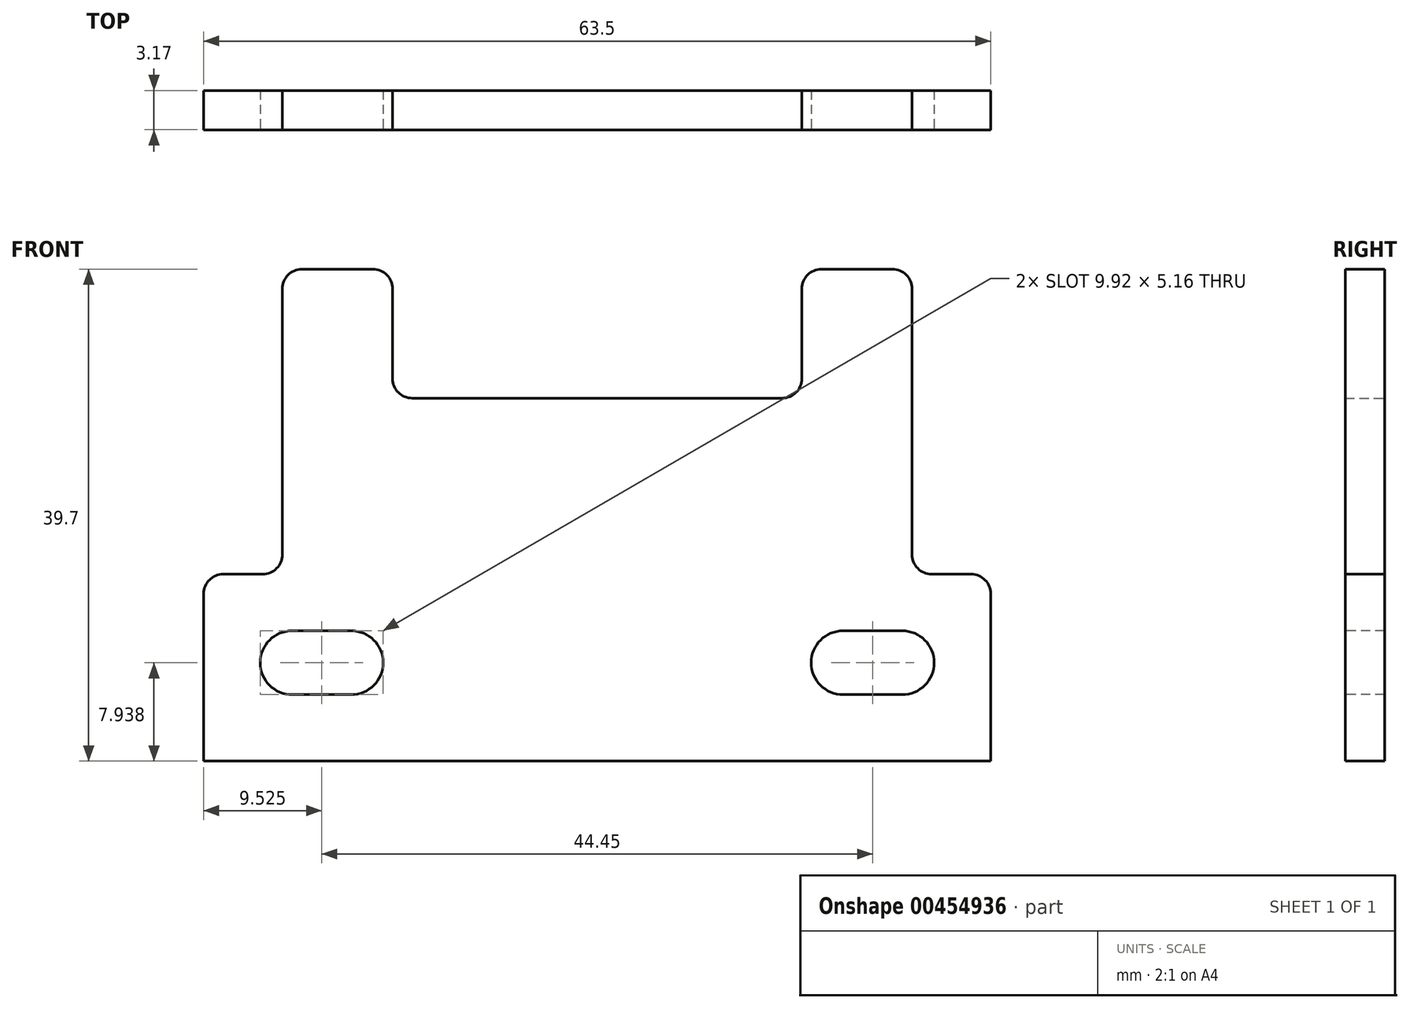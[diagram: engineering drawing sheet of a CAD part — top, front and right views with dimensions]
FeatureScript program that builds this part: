
annotation { "Feature Type Name" : "Feature", "Feature Type Description" : "" }
export const myFeature = defineFeature(function(context is Context, id is Id, definition is map)
    precondition{}
    {
        {
            var Q0;
            Q0=qCreatedBy(makeId("Front.planeOp"),FACE);
            var sketch = newSketch(context, id + "F0", { "sketchPlane" : qUnion([Q0])});
            skLineSegment(sketch, "E0", {"start": v(0, 0) * mm, "end": v(63.5, 0) * mm});
            skLineSegment(sketch, "E1", {"start": v(63.5, 0) * mm, "end": v(63.5, 15.08) * mm});
            skLineSegment(sketch, "E2", {"start": v(63.5, 15.08) * mm, "end": v(57.15, 15.08) * mm});
            skLineSegment(sketch, "E3", {"start": v(57.15, 15.08) * mm, "end": v(57.15, 39.7) * mm});
            skLineSegment(sketch, "E4", {"start": v(57.15, 39.7) * mm, "end": v(48.26, 39.7) * mm});
            skLineSegment(sketch, "E5", {"start": v(48.26, 39.7) * mm, "end": v(48.26, 29.29) * mm});
            skLineSegment(sketch, "E6", {"start": v(15.24, 29.29) * mm, "end": v(15.24, 39.7) * mm});
            skLineSegment(sketch, "E7", {"start": v(15.24, 39.7) * mm, "end": v(6.35, 39.7) * mm});
            skLineSegment(sketch, "E8", {"start": v(6.35, 39.7) * mm, "end": v(6.35, 15.08) * mm});
            skLineSegment(sketch, "E9", {"start": v(6.35, 15.08) * mm, "end": v(0, 15.08) * mm});
            skLineSegment(sketch, "E10", {"start": v(0, 15.08) * mm, "end": v(0, 0) * mm});
            skLineSegment(sketch, "E11", {"start": v(15.24, 29.29) * mm, "end": v(48.26, 29.29) * mm});
            skPoint(sketch, "E12.orphan", {"position": v(48.26, 15.08) * mm});
            skSolve(sketch);
        }
        {
            var Q0;
            Q0 = qSketchRegion(id + "F0", true);
            extrude(context, id + "F1", {"entities" : qUnion([Q0]), "depth" : 3.17 * mm});
        }
        {
            var Q0;
            Q0=makeQuery(id+"F1.opExtrude","SWEPT_EDGE",EDGE,{"disambiguationData":[OSD([sQuery(id+"F0.wireOp",EDGE,"E7"),sQuery(id+"F0.wireOp",EDGE,"E8")])]});
            var Q1;
            Q1=makeQuery(id+"F1.opExtrude","SWEPT_EDGE",EDGE,{"disambiguationData":[OSD([sQuery(id+"F0.wireOp",EDGE,"E8"),sQuery(id+"F0.wireOp",EDGE,"E9")])]});
            var Q2;
            Q2=makeQuery(id+"F1.opExtrude","SWEPT_EDGE",EDGE,{"disambiguationData":[OSD([sQuery(id+"F0.wireOp",EDGE,"E9"),sQuery(id+"F0.wireOp",EDGE,"E10")])]});
            var Q3;
            Q3=makeQuery(id+"F1.opExtrude","SWEPT_EDGE",EDGE,{"disambiguationData":[OSD([sQuery(id+"F0.wireOp",EDGE,"E6"),sQuery(id+"F0.wireOp",EDGE,"E7")])]});
            var Q4;
            Q4=makeQuery(id+"F1.opExtrude","SWEPT_EDGE",EDGE,{"disambiguationData":[OSD([sQuery(id+"F0.wireOp",EDGE,"1ljnW5oG-b6RX-7xke-IbpO-HqidATQd2flk"),sQuery(id+"F0.wireOp",EDGE,"E6")])]});
            var Q5;
            Q5=makeQuery(id+"F1.opExtrude","SWEPT_EDGE",EDGE,{"disambiguationData":[OSD([sQuery(id+"F0.wireOp",EDGE,"E5"),sQuery(id+"F0.wireOp",EDGE,"1ljnW5oG-b6RX-7xke-IbpO-HqidATQd2flk")])]});
            var Q6;
            Q6=makeQuery(id+"F1.opExtrude","SWEPT_EDGE",EDGE,{"disambiguationData":[OSD([sQuery(id+"F0.wireOp",EDGE,"E4"),sQuery(id+"F0.wireOp",EDGE,"E5")])]});
            var Q7;
            Q7=makeQuery(id+"F1.opExtrude","SWEPT_EDGE",EDGE,{"disambiguationData":[OSD([sQuery(id+"F0.wireOp",EDGE,"E3"),sQuery(id+"F0.wireOp",EDGE,"E4")])]});
            var Q8;
            Q8=makeQuery(id+"F1.opExtrude","SWEPT_EDGE",EDGE,{"disambiguationData":[OSD([sQuery(id+"F0.wireOp",EDGE,"E2"),sQuery(id+"F0.wireOp",EDGE,"E3")])]});
            var Q9;
            Q9=makeQuery(id+"F1.opExtrude","SWEPT_EDGE",EDGE,{"disambiguationData":[OSD([sQuery(id+"F0.wireOp",EDGE,"E1"),sQuery(id+"F0.wireOp",EDGE,"E2")])]});
            fillet(context, id + "F2", {"entities" : qUnion([Q0, Q1, Q2, Q3, Q4, Q5, Q6, Q7, Q8, Q9]), "radius" : 1.59 * mm, "tangentPropagation" : true, "allowEdgeOverflow" : false});
        }
        {
            var Q0;
            Q0=makeQuery(id+"F1.opExtrude","CAP_FACE",FACE,{"disambiguationData":[OSD([sQuery(id+"F0.wireOp",EDGE,"E0"),sQuery(id+"F0.wireOp",EDGE,"E1"),sQuery(id+"F0.wireOp",EDGE,"E2"),sQuery(id+"F0.wireOp",EDGE,"E3"),sQuery(id+"F0.wireOp",EDGE,"E4"),sQuery(id+"F0.wireOp",EDGE,"E5"),sQuery(id+"F0.wireOp",EDGE,"1ljnW5oG-b6RX-7xke-IbpO-HqidATQd2flk"),sQuery(id+"F0.wireOp",EDGE,"E6"),sQuery(id+"F0.wireOp",EDGE,"E7"),sQuery(id+"F0.wireOp",EDGE,"E8"),sQuery(id+"F0.wireOp",EDGE,"E9"),sQuery(id+"F0.wireOp",EDGE,"E10")])],"isStart":false});
            var sketch = newSketch(context, id + "F3", { "sketchPlane" : qUnion([Q0])});
            skArc(sketch, "E13", {"start": v(56.36, 5.36) * mm, "mid": v(58.93, 7.94) * mm, "end": v(56.36, 10.52) * mm});
            skArc(sketch, "E14", {"start": v(51.6, 10.52) * mm, "mid": v(49.02, 7.94) * mm, "end": v(51.6, 5.36) * mm});
            skLineSegment(sketch, "E15", {"start": v(51.6, 10.52) * mm, "end": v(56.36, 10.52) * mm});
            skLineSegment(sketch, "E16", {"start": v(51.6, 5.36) * mm, "end": v(56.36, 5.36) * mm});
            skArc(sketch, "E17", {"start": v(11.9, 5.36) * mm, "mid": v(14.48, 7.94) * mm, "end": v(11.9, 10.52) * mm});
            skPoint(sketch, "E17.centerSnap0", {"position": v(49.02, 7.94) * mm});
            skArc(sketch, "E18", {"start": v(7.14, 10.52) * mm, "mid": v(4.57, 7.94) * mm, "end": v(7.14, 5.36) * mm});
            skLineSegment(sketch, "E19", {"start": v(7.14, 10.52) * mm, "end": v(11.9, 10.52) * mm});
            skLineSegment(sketch, "E20", {"start": v(7.14, 5.36) * mm, "end": v(11.9, 5.36) * mm});
            skSolve(sketch);
        }
        {
            var Q0;
            Q0 = qSketchRegion(id + "F3", true);
            extrude(context, id + "F4", {"entities" : qUnion([Q0]), "operationType" : NewBodyOperationType.REMOVE, "oppositeDirection" : true, "depth" : 3.17 * mm});
        }
    });
